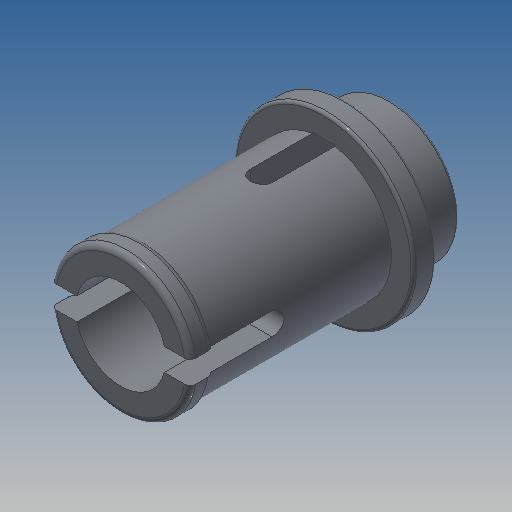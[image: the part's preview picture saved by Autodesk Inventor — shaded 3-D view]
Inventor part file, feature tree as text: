
AUTODESK INVENTOR PART (.ipt)
format: ipt  version: 2022.2 (Build 262287000, 287)  size: 280,576 bytes
history: native  units: mm (DEFAULTED — no unit token found)
features: sketch x2, extrude x2, revolve x1, fillet x1
ambient origin geometry x8: Origin, YZ Plane, XZ Plane, XY Plane, X Axis, Y Axis, Z Axis, Center Point
bodies: Solid2 (feature_tree)
feature tree (6):
  sketch  "Sketch1"  dims[d1=4.8mm d2=5.0mm d6=8.0mm]
  revolve  "Revolution1"  [1 undecoded]
  fillet  "Fillet1"  Radius=8.0mm
  extrude  "Extrusion1"  Depth=0.8mm
  extrude  "Extrusion2"  Depth=0.8mm
  sketch  "Sketch2"  dims[d7=0.8mm d8=6.4mm d9=0.8mm d14=0.8mm d19=8.0mm d20=90.0deg d21=4.8mm d22=0.0mm d25=10.0mm d26=0.0mm d27=0.2mm d28=0.1mm d29=0.0mm d30=0.0mm d32=3.4mm d33=1.6mm d34=3.4mm d35=0.8mm d36=0.0mm d37=3.2mm d38=4.8mm]
note: 1 required parameter value undecoded (feature->parameter linkage not recoverable at this tier; creation-order binding heuristic only, values carry confidence <= 0.55)
